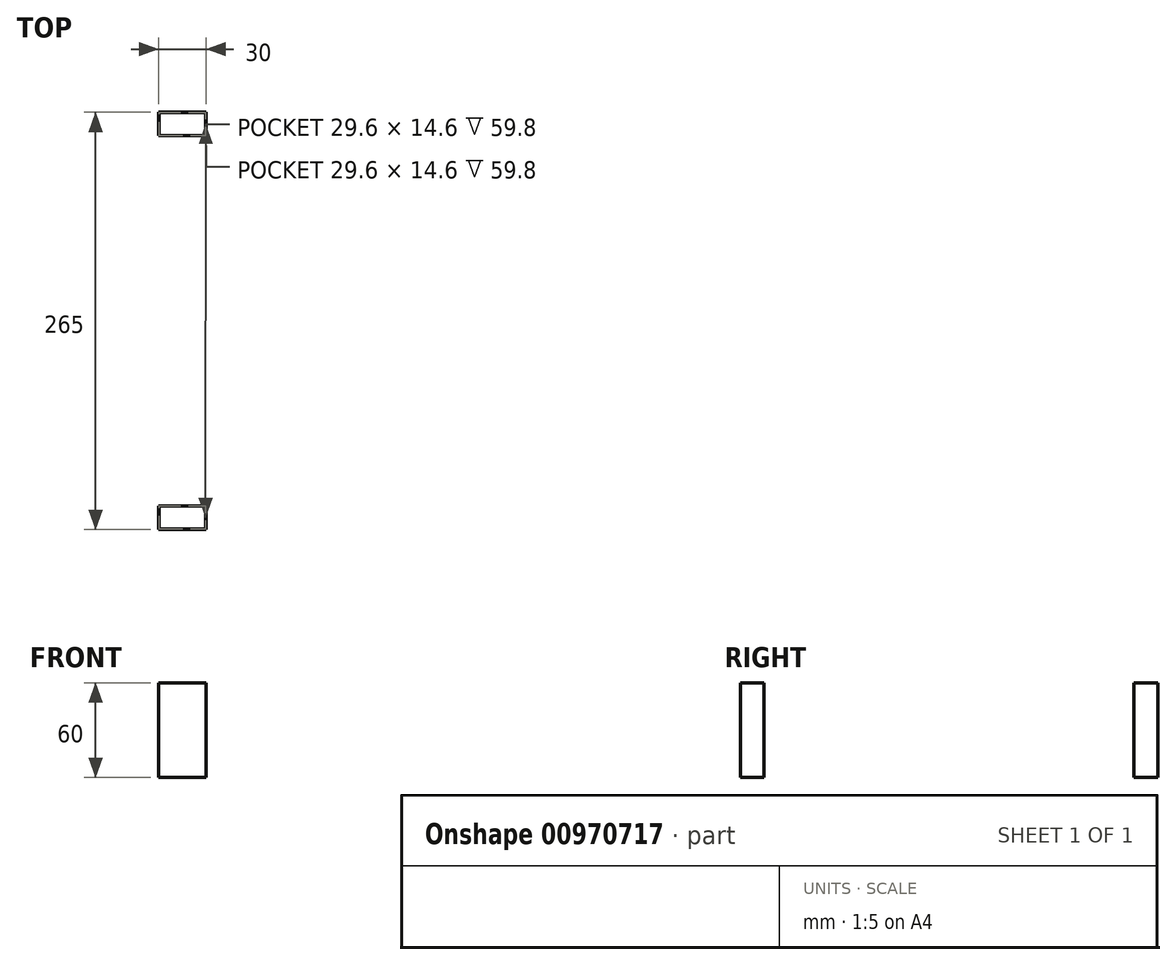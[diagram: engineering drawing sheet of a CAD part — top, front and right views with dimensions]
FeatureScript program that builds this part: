
annotation { "Feature Type Name" : "Feature", "Feature Type Description" : "" }
export const myFeature = defineFeature(function(context is Context, id is Id, definition is map)
    precondition{}
    {
        {
            var Q0;
            Q0=qCreatedBy(makeId("Top.planeOp"),FACE);
            var sketch = newSketch(context, id + "F0", { "sketchPlane" : qUnion([Q0])});
            skLineSegment(sketch, "E0.bottom", {"start": v(15, -7.5) * mm, "end": v(-15, -7.5) * mm});
            skLineSegment(sketch, "E0.top", {"start": v(15, 7.5) * mm, "end": v(-15, 7.5) * mm});
            skLineSegment(sketch, "E0.left", {"start": v(15, -7.5) * mm, "end": v(15, 7.5) * mm});
            skLineSegment(sketch, "E0.right", {"start": v(-15, -7.5) * mm, "end": v(-15, 7.5) * mm});
            skPoint(sketch, "E0.middle", {"position": v(0, 0) * mm});
            skLineSegment(sketch, "E1.0.1.0", {"start": v(15, 242.5) * mm, "end": v(15, 257.5) * mm});
            skPoint(sketch, "E1.0.1.1", {"position": v(0, 250) * mm});
            skLineSegment(sketch, "E1.0.1.2", {"start": v(15, 242.5) * mm, "end": v(-15, 242.5) * mm});
            skLineSegment(sketch, "E1.0.1.3", {"start": v(-15, 242.5) * mm, "end": v(-15, 257.5) * mm});
            skLineSegment(sketch, "E1.0.1.4", {"start": v(15, 257.5) * mm, "end": v(-15, 257.5) * mm});
            skLineSegment(sketch, "E1.direction1", {"start": v(-15, -7.5) * mm, "end": v(10, -7.5) * mm, "construction": true});
            skLineSegment(sketch, "E1.direction2", {"start": v(-15, -7.5) * mm, "end": v(-15, 242.5) * mm, "construction": true});
            skSolve(sketch);
        }
        {
            var Q0;
            Q0 = qSketchRegion(id + "F0", true);
            extrude(context, id + "F1", {"entities" : qUnion([Q0]), "depth" : 60 * mm, "offsetDistance" : 25 * mm});
        }
        {
            var Q0;
            Q0=makeQuery(id+"F1.opExtrude","CAP_FACE",FACE,{"disambiguationData":[OSD([sQuery(id+"F0.wireOp",EDGE,"E0.bottom"),sQuery(id+"F0.wireOp",EDGE,"E0.top"),sQuery(id+"F0.wireOp",EDGE,"E0.left"),sQuery(id+"F0.wireOp",EDGE,"E0.right")])],"isStart":false});
            var Q1;
            Q1=makeQuery(id+"F1.opExtrude","CAP_FACE",FACE,{"disambiguationData":[OSD([sQuery(id+"F0.wireOp",EDGE,"E1.0.1.0"),sQuery(id+"F0.wireOp",EDGE,"E1.0.1.2"),sQuery(id+"F0.wireOp",EDGE,"E1.0.1.3"),sQuery(id+"F0.wireOp",EDGE,"E1.0.1.4")])],"isStart":false});
            shell(context, id + "F2", {"entities" : qUnion([Q0, Q1]), "thickness" : 0.2 * mm});
        }
    });
